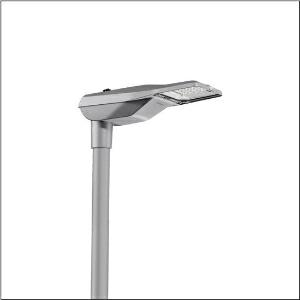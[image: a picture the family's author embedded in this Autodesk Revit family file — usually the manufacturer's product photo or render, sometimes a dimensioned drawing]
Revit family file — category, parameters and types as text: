
# Revit family: streetlight_sl_21_micro___stw1_0a_5xe1e43s08db_ea06
name_source: partatom
category: Lighting Fixtures
units: mm (PartAtom-declared; Revit-internal decimal feet)

## family parameters
Cut with Voids When Loaded = No
Host = Face
Light Source = No
Part Type = Normal
Room Calculation Point = No
Round Connector Dimension = Use Diameter
Shared = No

## types (1)
- --- (1 x LED, 5320 lm, 39.1 W, 4000K)
    Apparent Load = 39 VA
    CIE Flux Codes = 38 75 98 100 100
    Color Rendering = 70
    Color Temperature = 4000K
    Default Elevation = 1800 mm
    Description = Streetlight SL 21 micro, mast luminaire, primary light control with lens, of PMMA, primary optical cover: cover, of toughened safety glass, transparent, light distribution: STW1.0a, light emission: direct distribution, primary light characteristic: asymmetric, installation type: side-entry, post-top, LED, High Power LED, rated luminous flux: 5.320lm, luminous efficacy: 136lm/W, light colour: 740, colour temperature: 4000K, control: flexible luminous flux parameterisation, time-dependent luminous flux control, constant luminous flux control, overheat protection, pre-setting: logarithmic dimming characteristic, mains connection: 220..240V, AC, 50/60Hz, start of lifetime: 39W, end of service life: 41W, reduction: 18W, luminaire housing, of diecast aluminium, powder-coated, Siteco® metallic grey (DB 702S), corrosivity category C5 mid according to DIN EN ISO 12944, please order mast flange separately, inclination adjustable: 0°, 5°, 10°, 15°, sealing non-destructively replaceable, multi-level sealing system, length: 528mm, width: 235mm, height: 110mm, mast flange for spigot size: 42mm (side-entry): 5XC10008XM4, 60/48mm (side-entry/post-top): 5XC10108XM2, 76/60mm (side-entry/post-top): 5XC10108XM1, Smart Interface above, protection rating (complete): IP66, insulation class (complete): insulation class II (safety insulation), certification: CE, ENEC, ENEC+, VDE, impact resistance: IK09, permissible operating ambient temperature for outdoor applications: -40..+50°C, standard-compliant lighting for roads and squares, packaging unit: 1 piece

Light Distribution: STW1.0a
    Height = 110 mm
    Lamp = 1 x LED
    Lamp Light Flux = 5320 lm
    Lamp Power = 39.1 W
    Lamp count = 1
    Length = 528 mm
    Luminous efficacy = 136 lm/W
    Manufacturer = Siteco
    ModVariant = No
    Model = 5XE1E43S08DB
    Number of Poles = 1
    OnlyDefault = Yes
    Power Factor = 1
    Product Name = Streetlight SL 21 micro | STW1.0a
    Product group = mast luminaire | pylon top
    ProductGroupID = 6100
    Protection Class = Protection class II
    Protection Degree = IP 66
    RLX_Detail_Level = 1
    RLX_Emergency_Light_Flux = 0 lm
    RLX_Emergency_Type = 0
    RLX_Emergency_Type_DB = No
    RlxData = <blob elided: 98425 chars, md5=b13ba435>
    Socket = socket
    Standby Power = 0 W
    System Light Flux = 5320 lm
    System Power = 39 W
    Type Comments = factory setting: luminous flux: 100 % | dim-lin: 254 | 765 mA
    Type Image = l_1277292.jpg
    URL = http://relux.com
    VarID = @adj_125681
    Voltage = 0 V
    Weight = 0.00 kg
    Width = 235 mm

## geometry (parser evidence)
native form markers: Blend x4, Sweep x9
no freeform markers — native parametric forms only
